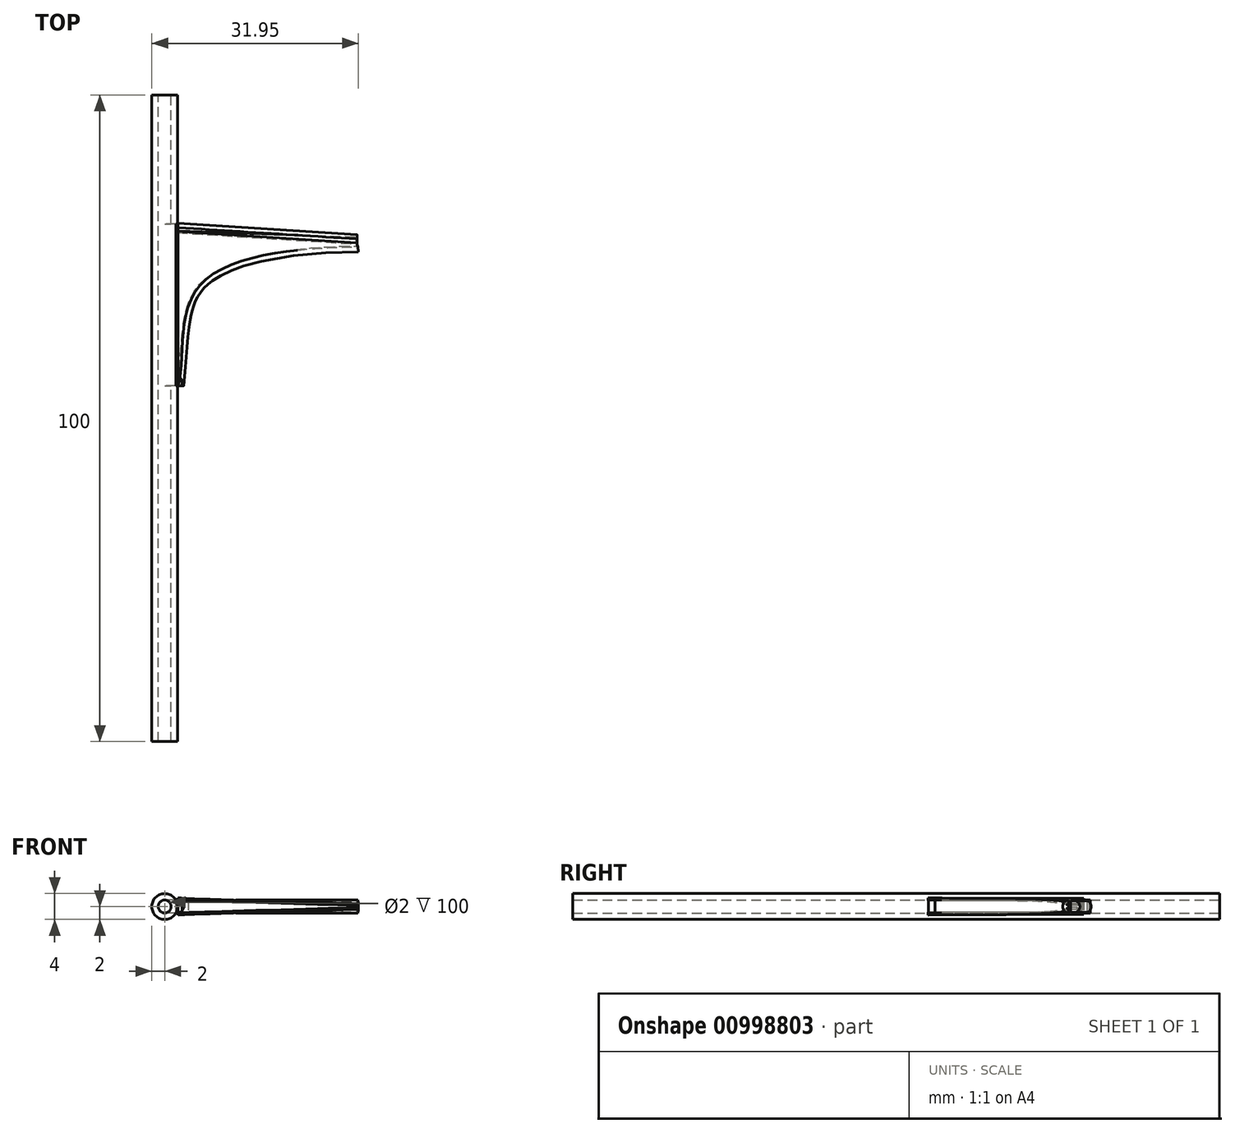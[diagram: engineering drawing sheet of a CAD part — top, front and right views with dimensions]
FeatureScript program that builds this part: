
annotation { "Feature Type Name" : "Feature", "Feature Type Description" : "" }
export const myFeature = defineFeature(function(context is Context, id is Id, definition is map)
    precondition{}
    {
        {
            var Q0;
            Q0=qCreatedBy(makeId("Front.planeOp"),FACE);
            var sketch = newSketch(context, id + "F0", { "sketchPlane" : qUnion([Q0])});
            skCircle(sketch, "E0", {"center": v(0, 0) * mm, "radius": 1 * mm});
            skCircle(sketch, "E1.0", {"center": v(0, 0) * mm, "radius": 2 * mm});
            skPoint(sketch, "E2", {"position": v(0, -1) * mm});
            skSolve(sketch);
        }
        {
            var Q0;
            Q0=qSketchRegion(id+"F0",true);
            extrude(context, id + "F1", {"entities" : qUnion([Q0]), "depth" : 100 * mm, "offsetDistance" : 25 * mm});
        }
        {
            var Q0;
            Q0=sQuery(id+"F0.wireOp",VERTEX,"E2");
            var Q1;
            Q1=sQuery(id+"F0.wireOp",EDGE,"E0");
            cPlane(context, id + "F2", {"entities" : qUnion([Q0, Q1]), "cplaneType" : CPlaneType.LINE_POINT, "offset" : 25 * mm, "width" : 150 * mm, "height" : 150 * mm});
        }
        {
            var Q0;
            Q0=qCreatedBy(id+"F2.planeOp",FACE);
            cPlane(context, id + "F3", {"entities" : qUnion([Q0]), "cplaneType" : CPlaneType.OFFSET, "offset" : 45 * mm, "width" : 150 * mm, "height" : 150 * mm});
        }
        {
            var Q0;
            Q0=qCreatedBy(id+"F3.planeOp",FACE);
            var sketch = newSketch(context, id + "F4", { "sketchPlane" : qUnion([Q0])});
            skLineSegment(sketch, "E3", {"start": v(0, -1) * mm, "end": v(1, -1) * mm, "construction": true});
            skLineSegment(sketch, "E4", {"start": v(0, 1) * mm, "end": v(1, 1) * mm, "construction": true});
            skLineSegment(sketch, "E5", {"start": v(1, -1) * mm, "end": v(1, 1) * mm});
            skSolve(sketch);
        }
        {
            var Q0;
            Q0=qSketchRegion(id+"F4",true);
            var Q1;
            Q1=sQuery(id+"F4.wireOp",EDGE,"E5");
            extrude(context, id + "F5", {"entities" : qUnion([Q0]), "bodyType" : ToolBodyType.SURFACE, "operationType" : NewBodyOperationType.REMOVE, "surfaceEntities" : qUnion([Q1]), "oppositeDirection" : true, "depth" : 25 * mm, "offsetDistance" : 25 * mm});
        }
        {
            var Q0;
            Q0=makeQuery(id+"F5.opExtrude","SWEPT_FACE",FACE,{"disambiguationData":[OSD([sQuery(id+"F4.wireOp",EDGE,"E5")])]});
            extrude(context, id + "F6", {"entities" : qUnion([Q0]), "operationType" : NewBodyOperationType.REMOVE, "oppositeDirection" : true, "depth" : 25 * mm, "offsetDistance" : 25 * mm, "hasSecondDirection" : true, "secondDirectionOppositeDirection" : false, "secondDirectionDepth" : 1 * mm});
        }
        {
            var Q0;
            Q0=makeQuery(id+"F6.boolean.opBoolean","INTERSECT",EDGE,{"derivedFrom":[makeQuery(id+"F1.opExtrude","SWEPT_FACE",FACE,{"disambiguationData":[OSD([sQuery(id+"F0.wireOp",EDGE,"E1.0")])]}),makeQuery(id+"F6.opExtrude","SWEPT_FACE",FACE,{"disambiguationData":[OSD([sQuery(id+"F4.wireOp",VERTEX,"E5.start")])]})]});
            var Q1;
            Q1=makeQuery(id+"F6.boolean.opBoolean","INTERSECT",EDGE,{"derivedFrom":[makeQuery(id+"F1.opExtrude","SWEPT_FACE",FACE,{"disambiguationData":[OSD([sQuery(id+"F0.wireOp",EDGE,"E1.0")])]}),makeQuery(id+"F6.opExtrude","SWEPT_FACE",FACE,{"disambiguationData":[OSD([sQuery(id+"F4.wireOp",VERTEX,"E5.end")])]})]});
            cPlane(context, id + "F7", {"entities" : qUnion([Q0, Q1]), "cplaneType" : CPlaneType.LINE_ANGLE, "offset" : 25 * mm, "angle" : 0 * degree, "width" : 150 * mm, "height" : 150 * mm});
        }
        {
            var Q0;
            Q0=qCreatedBy(id+"F7.planeOp",FACE);
            var sketch = newSketch(context, id + "F8", { "sketchPlane" : qUnion([Q0])});
            skLineSegment(sketch, "E6.bottom", {"start": v(-20, -1) * mm, "end": v(-45, -1) * mm});
            skLineSegment(sketch, "E6.top", {"start": v(-20, 1) * mm, "end": v(-45, 1) * mm});
            skLineSegment(sketch, "E6.left", {"start": v(-20, -1) * mm, "end": v(-20, 1) * mm});
            skLineSegment(sketch, "E6.right", {"start": v(-45, -1) * mm, "end": v(-45, 1) * mm});
            skLineSegment(sketch, "E7", {"start": v(-45, 0) * mm, "end": v(-20, 0) * mm});
            skLineSegment(sketch, "E8", {"start": v(-45, 0) * mm, "end": v(-41.17, 0) * mm});
            skLineSegment(sketch, "E9", {"start": v(-20, 0) * mm, "end": v(-24.2, 0) * mm});
            skSolve(sketch);
        }
        {
            var Q0;
            Q0=qSketchRegion(id+"F8",true);
            extrude(context, id + "F9", {"entities" : qUnion([Q0]), "depth" : 0.3 * mm, "offsetDistance" : 25 * mm});
        }
        {
            var Q0;
            Q0=makeQuery(id+"F9.opExtrude","CAP_FACE",FACE,{"disambiguationData":[OSD([sQuery(id+"F8.wireOp",EDGE,"E6.bottom"),sQuery(id+"F8.wireOp",EDGE,"E6.top"),sQuery(id+"F8.wireOp",EDGE,"E6.left"),sQuery(id+"F8.wireOp",EDGE,"E6.right")])],"isStart":false});
            var Q1;
            Q1=makeQuery(id+"F9.opExtrude","CAP_FACE",FACE,{"disambiguationData":[OSD([sQuery(id+"F8.wireOp",EDGE,"E6.bottom"),sQuery(id+"F8.wireOp",EDGE,"E6.top"),sQuery(id+"F8.wireOp",EDGE,"E6.left"),sQuery(id+"F8.wireOp",EDGE,"E6.right")])],"isStart":true});
            var Q2;
            Q2=makeQuery(id+"F9.opExtrude","SWEPT_BODY",BODY,{"disambiguationData":[OSD([sQuery(id+"F8.wireOp",EDGE,"E6.bottom"),sQuery(id+"F8.wireOp",EDGE,"E6.top"),sQuery(id+"F8.wireOp",EDGE,"E6.left"),sQuery(id+"F8.wireOp",EDGE,"E6.right")])]});
            shell(context, id + "F10", {"entities" : qUnion([Q0, Q1]), "parts" : qUnion([Q2]), "thickness" : 0.1 * mm});
        }
        {
            var Q0;
            Q0=makeQuery(id+"F9.opExtrude","SWEPT_FACE",FACE,{"disambiguationData":[OSD([sQuery(id+"F8.wireOp",EDGE,"E6.top")])]});
            var sketch = newSketch(context, id + "F11", { "sketchPlane" : qUnion([Q0])});
            skSolve(sketch);
        }
        {
            var Q0;
            Q0=sQuery(id+"F8.wireOp",EDGE,"E7");
            cPlane(context, id + "F12", {"entities" : qUnion([Q0]), "cplaneType" : CPlaneType.LINE_ANGLE, "offset" : 25 * mm, "angle" : 0 * degree, "width" : 150 * mm, "height" : 150 * mm});
        }
        {
            var Q0;
            Q0=makeQuery(id+"F9.opExtrude","CAP_FACE",FACE,{"disambiguationData":[OSD([sQuery(id+"F8.wireOp",EDGE,"E6.bottom"),sQuery(id+"F8.wireOp",EDGE,"E6.top"),sQuery(id+"F8.wireOp",EDGE,"E6.left"),sQuery(id+"F8.wireOp",EDGE,"E6.right")])],"isStart":false});
            var sketch = newSketch(context, id + "F13", { "sketchPlane" : qUnion([Q0])});
            skLineSegment(sketch, "E10.bottom", {"start": v(-44.9, -0.9) * mm, "end": v(-20.1, -0.9) * mm});
            skLineSegment(sketch, "E10.top", {"start": v(-44.9, 0.9) * mm, "end": v(-20.1, 0.9) * mm});
            skLineSegment(sketch, "E10.left", {"start": v(-44.9, -0.9) * mm, "end": v(-44.9, 0.9) * mm});
            skLineSegment(sketch, "E10.right", {"start": v(-20.1, -0.9) * mm, "end": v(-20.1, 0.9) * mm});
            skSolve(sketch);
        }
        {
            var Q0;
            Q0=makeQuery(id+"F13.imprint","IMPRINT",FACE,{"disambiguationData":[TD([[makeQuery(id+"F13.imprint","IMPRINT",EDGE,{"derivedFrom":sQuery(id+"F13.wireOp",EDGE,"E10.bottom")}),-1.0]])]});
            extrude(context, id + "F14", {"entities" : qUnion([Q0]), "operationType" : NewBodyOperationType.REMOVE, "oppositeDirection" : true, "depth" : 2 * mm, "offsetDistance" : 25 * mm});
        }
        {
            var Q0;
            Q0=makeQuery(id+"F9.opExtrude","CAP_EDGE",EDGE,{"disambiguationData":[OSD([sQuery(id+"F8.wireOp",EDGE,"E6.right")])],"isStart":false});
            cPlane(context, id + "F15", {"entities" : qUnion([Q0]), "cplaneType" : CPlaneType.LINE_ANGLE, "offset" : 25 * mm, "angle" : 90 * degree, "width" : 150 * mm, "height" : 150 * mm});
        }
        {
            var Q0;
            Q0=qCreatedBy(id+"F15.planeOp",FACE);
            var sketch = newSketch(context, id + "F16", { "sketchPlane" : qUnion([Q0])});
            skArc(sketch, "E11", {"start": v(-2.03, 1) * mm, "mid": v(-2.93, 0) * mm, "end": v(-2.03, -1) * mm});
            skPoint(sketch, "E12", {"position": v(-2.93, 0) * mm});
            skLineSegment(sketch, "E13", {"start": v(-2.03, -1) * mm, "end": v(-2.03, 1) * mm});
            skSolve(sketch);
        }
        {
            var Q0;
            Q0=qCreatedBy(id+"F12.planeOp",FACE);
            var sketch = newSketch(context, id + "F17", { "sketchPlane" : qUnion([Q0])});
            skFitSpline(sketch, "E14", {"points": [v(2.24, -44.99) * mm, v(5.83, -29.16) * mm, v(29.88, -23.58) * mm], "startDerivative": vector(5.62, 52.74) * mm, "endDerivative": vector(56.37, 0.2) * mm});
            skSolve(sketch);
        }
        {
            var Q0;
            Q0=makeQuery(id+"F16.imprint","IMPRINT",FACE,{"disambiguationData":[TD([[makeQuery(id+"F16.imprint","IMPRINT",EDGE,{"derivedFrom":sQuery(id+"F16.wireOp",EDGE,"E11")}),1.0]])]});
            var Q1;
            Q1=qConstructionFilter(qBodyType(qCreatedBy(id+"F17",EDGE),BodyType.WIRE),ConstructionObject.NO);
            sweep(context, id + "F18", {"profiles" : qUnion([Q0]), "path" : qUnion([Q1])});
        }
        {
            var Q0;
            Q0=makeQuery(id+"F18.opSweep","CAP_FACE",FACE,{"disambiguationData":[OSD([sQuery(id+"F16.wireOp",EDGE,"E11"),sQuery(id+"F16.wireOp",EDGE,"WA85A7l2-u0vf-G9TA-IQFj-N9G0mvhgZiK2"),sQuery(id+"F17.wireOp",VERTEX,"E14.start")])],"isStart":true});
            var sketch = newSketch(context, id + "F19", { "sketchPlane" : qUnion([Q0])});
            skLineSegment(sketch, "E15.bottom", {"start": v(2.03, -1) * mm, "end": v(2.66, -1) * mm});
            skLineSegment(sketch, "E15.top", {"start": v(2.03, 1) * mm, "end": v(2.66, 1) * mm});
            skLineSegment(sketch, "E15.left", {"start": v(2.03, -1) * mm, "end": v(2.03, 1) * mm});
            skLineSegment(sketch, "E15.right", {"start": v(2.66, -1) * mm, "end": v(2.66, 1) * mm});
            skSolve(sketch);
        }
        {
            var Q0;
            Q0=qSketchRegion(id+"F19",true);
            var Q1;
            {var subQ1=sQuery(id+"F17.wireOp",VERTEX,"E14.start");var subQ2=makeQuery(id+"F18.opSweep","CAP_EDGE",EDGE,{"disambiguationData":[OSD([sQuery(id+"F16.wireOp",EDGE,"WA85A7l2-u0vf-G9TA-IQFj-N9G0mvhgZiK2"),subQ1])],"isStart":true});var subQ5=sQuery(id+"F19.wireOp",EDGE,"E15.right");var subQ6=makeQuery(id+"F19.imprint","INTERSECT",VERTEX,{"disambiguationData":[OD(0.0)],"derivedFrom":[subQ2,subQ5]});Q1=makeQuery(id+"F19.imprint","IMPRINT",FACE,{"disambiguationData":[TD([[makeQuery(id+"F19.imprint","IMPRINT",EDGE,{"disambiguationData":[TD([[subQ6,-1.0]])],"derivedFrom":subQ5}),1.0]])]});}
            extrude(context, id + "F20", {"entities" : qUnion([Q0, Q1]), "oppositeDirection" : true, "depth" : 1 * mm, "offsetDistance" : 25 * mm});
        }
        {
            var Q0;
            Q0=makeQuery(id+"F13.imprint","IMPRINT",FACE,{"disambiguationData":[TD([[makeQuery(id+"F13.imprint","IMPRINT",EDGE,{"derivedFrom":sQuery(id+"F13.wireOp",EDGE,"E10.bottom")}),1.0]])]});
            var sketch = newSketch(context, id + "F21", { "sketchPlane" : qUnion([Q0])});
            skLineSegment(sketch, "E16", {"start": v(-21.33, -0.83) * mm, "end": v(-21.33, 0.8) * mm});
            skArc(sketch, "E17", {"start": v(-21.33, -0.83) * mm, "mid": v(-19.86, 0) * mm, "end": v(-21.33, 0.8) * mm});
            skSolve(sketch);
        }
        {
            var Q0;
            Q0=qCreatedBy(id+"F12.planeOp",FACE);
            var sketch = newSketch(context, id + "F22", { "sketchPlane" : qUnion([Q0])});
            skLineSegment(sketch, "E18", {"start": v(2, -20.1) * mm, "end": v(29.74, -21.85) * mm});
            skSolve(sketch);
        }
        {
            var Q0;
            {var subQ0=sQuery(id+"F21.wireOp",EDGE,"E17");var subQ1=sQuery(id+"F21.wireOp",EDGE,"E16");var subQ2=makeQuery(id+"F21.imprint","INTERSECT",VERTEX,{"disambiguationData":[OD(1.0)],"derivedFrom":[subQ1,subQ0]});Q0=makeQuery(id+"F21.imprint","IMPRINT",FACE,{"disambiguationData":[TD([[makeQuery(id+"F21.imprint","IMPRINT",EDGE,{"disambiguationData":[TD([[subQ2,1.0]])],"derivedFrom":subQ1}),-1.0]])]});}
            var Q1;
            {var subQ0=sQuery(id+"F21.wireOp",EDGE,"E17");var subQ1=makeQuery(id+"F13.imprint","IMPRINT",EDGE,{"derivedFrom":makeQuery(id+"F9.opExtrude","CAP_EDGE",EDGE,{"disambiguationData":[OSD([sQuery(id+"F8.wireOp",EDGE,"E6.left")])],"isStart":false})});var subQ2=makeQuery(id+"F21.imprint","INTERSECT",VERTEX,{"disambiguationData":[OD(0.0)],"derivedFrom":[subQ1,subQ0]});Q1=makeQuery(id+"F21.imprint","IMPRINT",FACE,{"disambiguationData":[TD([[makeQuery(id+"F21.imprint","IMPRINT",EDGE,{"disambiguationData":[TD([[subQ2,1.0]])],"derivedFrom":subQ0}),1.0]])]});}
            var Q2;
            {var subQ0=sQuery(id+"F21.wireOp",EDGE,"E17");var subQ1=makeQuery(id+"F13.imprint","IMPRINT",EDGE,{"derivedFrom":makeQuery(id+"F9.opExtrude","CAP_EDGE",EDGE,{"disambiguationData":[OSD([sQuery(id+"F8.wireOp",EDGE,"E6.left")])],"isStart":false})});var subQ2=makeQuery(id+"F21.imprint","INTERSECT",VERTEX,{"disambiguationData":[OD(0.0)],"derivedFrom":[subQ1,subQ0]});Q2=makeQuery(id+"F21.imprint","IMPRINT",FACE,{"disambiguationData":[TD([[makeQuery(id+"F21.imprint","IMPRINT",EDGE,{"disambiguationData":[TD([[subQ2,-1.0]])],"derivedFrom":subQ0}),1.0]])]});}
            var Q3;
            Q3=sQuery(id+"F22.wireOp",EDGE,"E18");
            sweep(context, id + "F23", {"profiles" : qUnion([Q0, Q1, Q2]), "path" : qUnion([Q3])});
        }
        {
            var Q0;
            Q0=makeQuery(id+"F18.opSweep","CAP_FACE",FACE,{"disambiguationData":[OSD([sQuery(id+"F16.wireOp",EDGE,"E11"),sQuery(id+"F16.wireOp",EDGE,"E13"),sQuery(id+"F17.wireOp",VERTEX,"E14.end")])],"isStart":false});
            var sketch = newSketch(context, id + "F24", { "sketchPlane" : qUnion([Q0])});
            skPoint(sketch, "E19", {"position": v(-26.5, 0.15) * mm});
            skPoint(sketch, "E20", {"position": v(-26.16, 0.15) * mm});
            skPoint(sketch, "E21", {"position": v(-26.5, -0.14) * mm});
            skPoint(sketch, "E22", {"position": v(-26.17, -0.14) * mm});
            skSolve(sketch);
        }
        {
            var Q0;
            Q0=sQuery(id+"F24.wireOp",VERTEX,"E19");
            var Q1;
            Q1=sQuery(id+"F24.wireOp",VERTEX,"E20");
            var Q2;
            Q2=makeQuery(id+"F20.opExtrude","CAP_VERTEX",VERTEX,{"disambiguationData":[OSD([sQuery(id+"F19.wireOp",EDGE,"E15.top"),sQuery(id+"F19.wireOp",EDGE,"E15.right")])],"isStart":true});
            cPlane(context, id + "F25", {"entities" : qUnion([Q0, Q1, Q2]), "cplaneType" : CPlaneType.THREE_POINT, "offset" : 25 * mm, "width" : 150 * mm, "height" : 150 * mm});
        }
        {
            var Q0;
            Q0=qCreatedBy(id+"F25.planeOp",FACE);
            var sketch = newSketch(context, id + "F26", { "sketchPlane" : qUnion([Q0])});
            skFitSpline(sketch, "E23", {"points": [v(2.02, 45.07) * mm, v(6.2, 28.67) * mm, v(29.85, 23.53) * mm, v(30, 23.6) * mm], "startDerivative": vector(8.72, -29.77) * mm, "endDerivative": vector(-18.29, 4.9) * mm});
            skLineSegment(sketch, "E24", {"start": v(2.03, 45.07) * mm, "end": v(2.02, 45.07) * mm});
            skLineSegment(sketch, "E25", {"start": v(2.03, 45.07) * mm, "end": v(2.02, 21.03) * mm});
            skLineSegment(sketch, "E26", {"start": v(29.4, 22.02) * mm, "end": v(29.85, 23.53) * mm});
            skLineSegment(sketch, "E27", {"start": v(29.4, 22.02) * mm, "end": v(2.02, 21.03) * mm});
            skLineSegment(sketch, "E28.bottom", {"start": v(2.02, 21.03) * mm, "end": v(1.9, 21.03) * mm});
            skLineSegment(sketch, "E28.top", {"start": v(2.02, 45.07) * mm, "end": v(1.9, 45.07) * mm});
            skLineSegment(sketch, "E28.left", {"start": v(2.02, 21.03) * mm, "end": v(2.02, 45.07) * mm});
            skLineSegment(sketch, "E28.right", {"start": v(1.9, 21.03) * mm, "end": v(1.9, 45.07) * mm});
            skSolve(sketch);
        }
        {
            var Q0;
            {var subQ0=sQuery(id+"F26.wireOp",EDGE,"E24");Q0=makeQuery(id+"F26.imprint","IMPRINT",FACE,{"disambiguationData":[TD([[makeQuery(id+"F26.imprint","IMPRINT",EDGE,{"derivedFrom":subQ0}),1.0]])]});}
            var Q1;
            {var subQ0=sQuery(id+"F26.wireOp",EDGE,"E26");Q1=makeQuery(id+"F26.imprint","IMPRINT",FACE,{"disambiguationData":[TD([[makeQuery(id+"F26.imprint","IMPRINT",EDGE,{"derivedFrom":subQ0}),1.0]])]});}
            extrude(context, id + "F27", {"entities" : qUnion([Q0, Q1]), "oppositeDirection" : true, "depth" : 0.3 * mm, "offsetDistance" : 25 * mm});
        }
        {
            var Q0;
            Q0=makeQuery(id+"F27.opExtrude","SWEPT_BODY",BODY,{"disambiguationData":[OSD([sQuery(id+"F26.wireOp",EDGE,"E23"),sQuery(id+"F26.wireOp",EDGE,"E24"),sQuery(id+"F26.wireOp",EDGE,"E25"),sQuery(id+"F26.wireOp",EDGE,"uEauQ0tK-GSql-IQPN-dBZD-K6hnNpkl1m4U"),sQuery(id+"F26.wireOp",EDGE,"E26")])]});
            var Q1;
            Q1=makeQuery(id+"F27.opExtrude","SWEPT_BODY",BODY,{"disambiguationData":[OSD([sQuery(id+"F26.wireOp",EDGE,"E23"),sQuery(id+"F26.wireOp",EDGE,"E25"),sQuery(id+"F26.wireOp",EDGE,"E26"),sQuery(id+"F26.wireOp",EDGE,"E27")])]});
            var Q2;
            Q2=qCreatedBy(id+"F12.planeOp",FACE);
            mirror(context, id + "F28", {"entities" : qUnion([Q0, Q1]), "mirrorPlane" : qUnion([Q2])});
        }
        {
            var Q0;
            Q0=makeQuery(id+"F9.opExtrude","CAP_FACE",FACE,{"disambiguationData":[OSD([sQuery(id+"F8.wireOp",EDGE,"E6.bottom"),sQuery(id+"F8.wireOp",EDGE,"E6.top"),sQuery(id+"F8.wireOp",EDGE,"E6.left"),sQuery(id+"F8.wireOp",EDGE,"E6.right")])],"isStart":false});
            var sketch = newSketch(context, id + "F29", { "sketchPlane" : qUnion([Q0])});
            skLineSegment(sketch, "E29.bottom", {"start": v(-20.1, -0.9) * mm, "end": v(-20.47, -0.9) * mm});
            skLineSegment(sketch, "E29.top", {"start": v(-20.1, 0.9) * mm, "end": v(-20.47, 0.9) * mm});
            skLineSegment(sketch, "E29.left", {"start": v(-20.1, -0.9) * mm, "end": v(-20.1, 0.9) * mm});
            skLineSegment(sketch, "E29.right", {"start": v(-20.47, -0.9) * mm, "end": v(-20.47, 0.9) * mm});
            skSolve(sketch);
        }
        {
            var Q0;
            Q0 = qSketchRegion(id + "F29", true);
            extrude(context, id + "F30", {"entities" : qUnion([Q0]), "operationType" : NewBodyOperationType.ADD, "oppositeDirection" : true, "depth" : 0.1 * mm, "offsetDistance" : 25 * mm});
        }
        {
            var Q0;
            Q0=makeQuery(id+"F28.opPattern","COPY",FACE,{"derivedFrom":makeQuery(id+"F27.opExtrude","SWEPT_FACE",FACE,{"disambiguationData":[OSD([sQuery(id+"F26.wireOp",EDGE,"E27")])]}),"instanceName":"1"});
            var sketch = newSketch(context, id + "F31", { "sketchPlane" : qUnion([Q0])});
            skLineSegment(sketch, "E30.bottom", {"start": v(-2.82, 1.03) * mm, "end": v(-4.42, 1.03) * mm});
            skLineSegment(sketch, "E30.top", {"start": v(-2.82, -0.85) * mm, "end": v(-4.42, -0.85) * mm});
            skLineSegment(sketch, "E30.left", {"start": v(-2.82, 1.03) * mm, "end": v(-2.82, -0.85) * mm});
            skLineSegment(sketch, "E30.right", {"start": v(-4.42, 1.03) * mm, "end": v(-4.42, -0.85) * mm});
            skSolve(sketch);
        }
        {
            var Q0;
            Q0 = qSketchRegion(id + "F31", true);
            extrude(context, id + "F32", {"entities" : qUnion([Q0]), "oppositeDirection" : true, "depth" : 0.1 * mm, "offsetDistance" : 25 * mm});
        }
        {
            var Q0;
            Q0=makeQuery(id+"F26.imprint","IMPRINT",FACE,{"disambiguationData":[TD([[makeQuery(id+"F26.imprint","IMPRINT",EDGE,{"derivedFrom":sQuery(id+"F26.wireOp",EDGE,"E28.bottom")}),-1.0]])]});
            extrude(context, id + "F33", {"entities" : qUnion([Q0]), "depth" : 0.1 * mm, "offsetDistance" : 25 * mm});
        }
        {
            var Q0;
            Q0=makeQuery(id+"F33.opExtrude","SWEPT_BODY",BODY,{"disambiguationData":[OSD([sQuery(id+"F26.wireOp",EDGE,"E28.bottom"),sQuery(id+"F26.wireOp",EDGE,"E28.top"),sQuery(id+"F26.wireOp",EDGE,"E28.left"),sQuery(id+"F26.wireOp",EDGE,"E28.right")])]});
            var Q1;
            Q1=qCreatedBy(id+"F12.planeOp",FACE);
            mirror(context, id + "F34", {"entities" : qUnion([Q0]), "mirrorPlane" : qUnion([Q1])});
        }
    });
